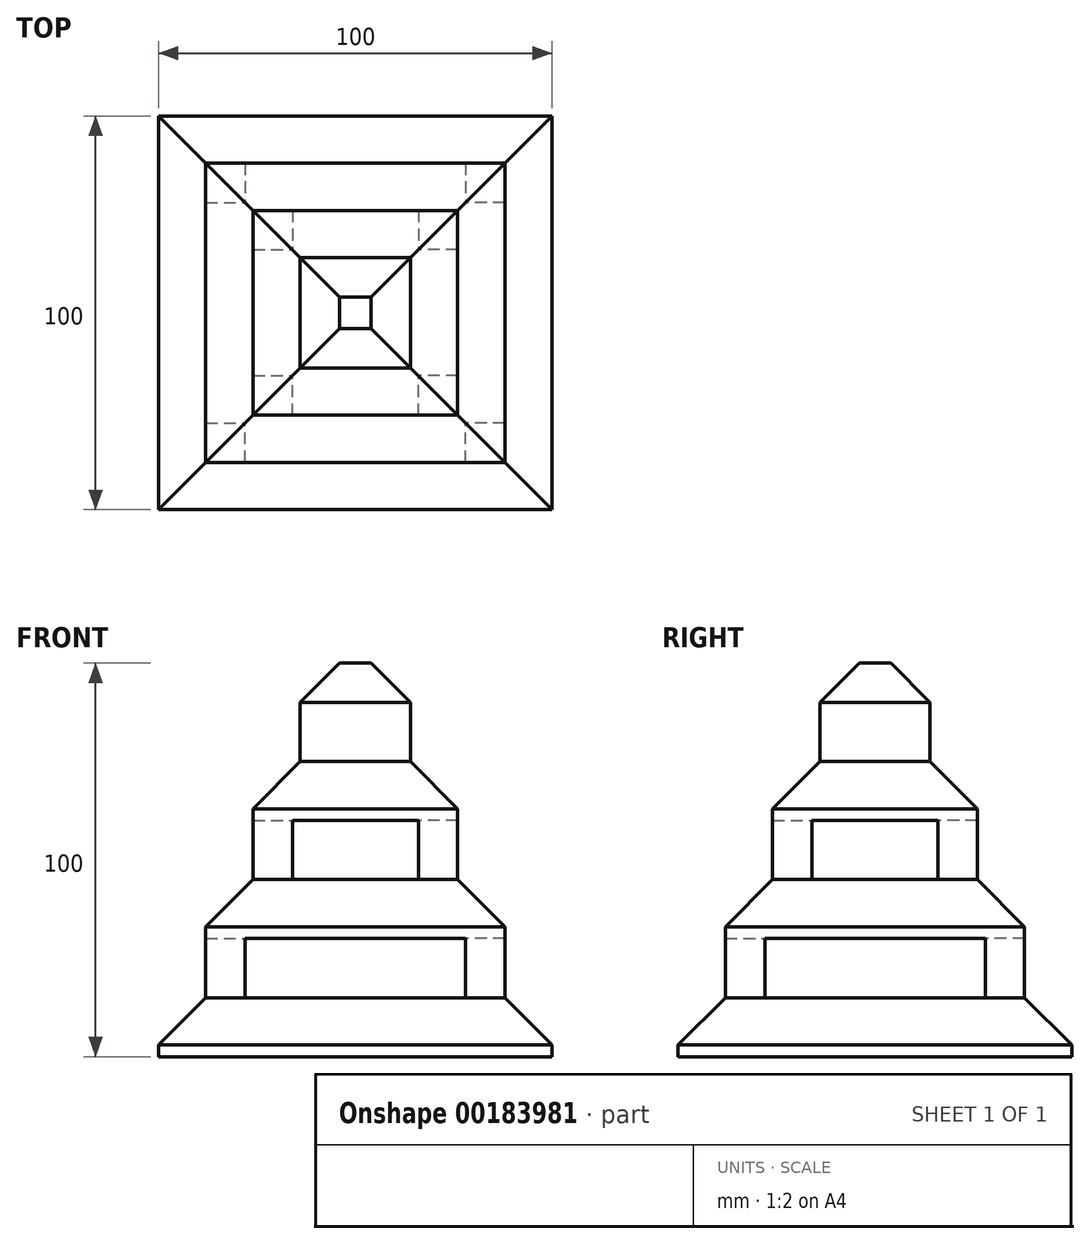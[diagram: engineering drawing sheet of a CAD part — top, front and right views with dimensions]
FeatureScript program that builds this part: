
annotation { "Feature Type Name" : "Feature", "Feature Type Description" : "" }
export const myFeature = defineFeature(function(context is Context, id is Id, definition is map)
    precondition{}
    {
        {
            var Q0;
            Q0=qCreatedBy(makeId("Top.planeOp"),FACE);
            var sketch = newSketch(context, id + "F0", { "sketchPlane" : qUnion([Q0])});
            skLineSegment(sketch, "E0.bottom", {"start": v(-50, 50) * mm, "end": v(50, 50) * mm});
            skLineSegment(sketch, "E0.top", {"start": v(-50, -50) * mm, "end": v(50, -50) * mm});
            skLineSegment(sketch, "E0.left", {"start": v(-50, 50) * mm, "end": v(-50, -50) * mm});
            skLineSegment(sketch, "E0.right", {"start": v(50, 50) * mm, "end": v(50, -50) * mm});
            skPoint(sketch, "E0.middle", {"position": v(0, 0) * mm});
            skSolve(sketch);
        }
        {
            var Q0;
            Q0 = qSketchRegion(id + "F0", true);
            extrude(context, id + "F1", {"entities" : qUnion([Q0]), "depth" : 15 * mm});
        }
        {
            var Q0;
            Q0=makeQuery(id+"F1.opExtrude","CAP_FACE",FACE,{"disambiguationData":[OSD([sQuery(id+"F0.wireOp",EDGE,"E0.bottom"),sQuery(id+"F0.wireOp",EDGE,"E0.top"),sQuery(id+"F0.wireOp",EDGE,"E0.left"),sQuery(id+"F0.wireOp",EDGE,"E0.right")])],"isStart":false});
            chamfer(context, id + "F2", {"entities" : qUnion([Q0]), "width" : 12 * mm, "tangentPropagation" : true});
        }
        {
            var Q0;
            Q0=makeQuery(id+"F1.opExtrude","CAP_FACE",FACE,{"disambiguationData":[OSD([sQuery(id+"F0.wireOp",EDGE,"E0.bottom"),sQuery(id+"F0.wireOp",EDGE,"E0.top"),sQuery(id+"F0.wireOp",EDGE,"E0.left"),sQuery(id+"F0.wireOp",EDGE,"E0.right")])],"isStart":false});
            var sketch = newSketch(context, id + "F3", { "sketchPlane" : qUnion([Q0])});
            skLineSegment(sketch, "E1.bottom", {"start": v(-38, 38) * mm, "end": v(-28, 38) * mm});
            skLineSegment(sketch, "E1.top", {"start": v(-38, 28) * mm, "end": v(-28, 28) * mm});
            skLineSegment(sketch, "E1.left", {"start": v(-38, 38) * mm, "end": v(-38, 28) * mm});
            skLineSegment(sketch, "E1.right", {"start": v(-28, 38) * mm, "end": v(-28, 28) * mm});
            skLineSegment(sketch, "E2.bottom", {"start": v(38, 38) * mm, "end": v(28, 38) * mm});
            skLineSegment(sketch, "E2.top", {"start": v(38, 28) * mm, "end": v(28, 28) * mm});
            skLineSegment(sketch, "E2.left", {"start": v(38, 38) * mm, "end": v(38, 28) * mm});
            skLineSegment(sketch, "E2.right", {"start": v(28, 38) * mm, "end": v(28, 28) * mm});
            skLineSegment(sketch, "E3.bottom", {"start": v(38, -38) * mm, "end": v(28, -38) * mm});
            skLineSegment(sketch, "E3.top", {"start": v(38, -28) * mm, "end": v(28, -28) * mm});
            skLineSegment(sketch, "E3.left", {"start": v(38, -38) * mm, "end": v(38, -28) * mm});
            skLineSegment(sketch, "E3.right", {"start": v(28, -38) * mm, "end": v(28, -28) * mm});
            skLineSegment(sketch, "E4.bottom", {"start": v(-38, -38) * mm, "end": v(-28, -38) * mm});
            skLineSegment(sketch, "E4.top", {"start": v(-38, -28) * mm, "end": v(-28, -28) * mm});
            skLineSegment(sketch, "E4.left", {"start": v(-38, -38) * mm, "end": v(-38, -28) * mm});
            skLineSegment(sketch, "E4.right", {"start": v(-28, -38) * mm, "end": v(-28, -28) * mm});
            skSolve(sketch);
        }
        {
            var Q0;
            Q0=makeQuery(id+"F3.imprint","IMPRINT",FACE,{"disambiguationData":[TD([[makeQuery(id+"F3.imprint","IMPRINT",EDGE,{"derivedFrom":sQuery(id+"F3.wireOp",EDGE,"E1.bottom")}),1.0]])]});
            var Q1;
            Q1=makeQuery(id+"F3.imprint","IMPRINT",FACE,{"disambiguationData":[TD([[makeQuery(id+"F3.imprint","IMPRINT",EDGE,{"derivedFrom":sQuery(id+"F3.wireOp",EDGE,"E2.bottom")}),1.0]])]});
            var Q2;
            Q2=makeQuery(id+"F3.imprint","IMPRINT",FACE,{"disambiguationData":[TD([[makeQuery(id+"F3.imprint","IMPRINT",EDGE,{"derivedFrom":sQuery(id+"F3.wireOp",EDGE,"E3.bottom")}),1.0]])]});
            var Q3;
            Q3=makeQuery(id+"F3.imprint","IMPRINT",FACE,{"disambiguationData":[TD([[makeQuery(id+"F3.imprint","IMPRINT",EDGE,{"derivedFrom":sQuery(id+"F3.wireOp",EDGE,"E4.bottom")}),1.0]])]});
            extrude(context, id + "F4", {"entities" : qUnion([Q0, Q1, Q2, Q3]), "operationType" : NewBodyOperationType.ADD, "depth" : 15 * mm});
        }
        {
            var Q0;
            Q0=makeQuery(id+"F4.opExtrude","CAP_FACE",FACE,{"disambiguationData":[OSD([sQuery(id+"F3.wireOp",EDGE,"E1.bottom"),sQuery(id+"F3.wireOp",EDGE,"E1.top"),sQuery(id+"F3.wireOp",EDGE,"E1.left"),sQuery(id+"F3.wireOp",EDGE,"E1.right")])],"isStart":false});
            var sketch = newSketch(context, id + "F5", { "sketchPlane" : qUnion([Q0])});
            skLineSegment(sketch, "E5.bottom", {"start": v(-38, 38) * mm, "end": v(38, 38) * mm});
            skLineSegment(sketch, "E5.top", {"start": v(-38, -38) * mm, "end": v(38, -38) * mm});
            skLineSegment(sketch, "E5.left", {"start": v(-38, 38) * mm, "end": v(-38, -38) * mm});
            skLineSegment(sketch, "E5.right", {"start": v(38, 38) * mm, "end": v(38, -38) * mm});
            skSolve(sketch);
        }
        {
            var Q0;
            {var subQ3=sQuery(id+"F5.wireOp",EDGE,"E5.top");Q0=makeQuery(id+"F5.imprint","IMPRINT",FACE,{"disambiguationData":[TD([[makeQuery(id+"F5.imprint","IMPRINT",EDGE,{"derivedFrom":subQ3}),1.0]])]});}
            var Q1;
            {var subQ4=makeQuery(id+"F4.opExtrude","CAP_EDGE",EDGE,{"disambiguationData":[OSD([sQuery(id+"F3.wireOp",EDGE,"E1.top")])],"isStart":false});Q1=makeQuery(id+"F5.imprint","IMPRINT",FACE,{"disambiguationData":[TD([[makeQuery(id+"F5.imprint","IMPRINT",EDGE,{"derivedFrom":subQ4}),1.0]])]});}
            extrude(context, id + "F6", {"entities" : qUnion([Q0, Q1]), "operationType" : NewBodyOperationType.ADD, "depth" : 15 * mm});
        }
        {
            var Q0;
            Q0=makeQuery(id+"F6.opExtrude","CAP_FACE",FACE,{"disambiguationData":[OSD([sQuery(id+"F5.wireOp",EDGE,"E5.bottom"),sQuery(id+"F5.wireOp",EDGE,"E5.top"),sQuery(id+"F5.wireOp",EDGE,"E5.left"),sQuery(id+"F5.wireOp",EDGE,"E5.right")])],"isStart":false});
            chamfer(context, id + "F7", {"entities" : qUnion([Q0]), "width" : 12 * mm, "tangentPropagation" : true});
        }
        {
            var Q0;
            Q0=makeQuery(id+"F6.opExtrude","CAP_FACE",FACE,{"disambiguationData":[OSD([sQuery(id+"F5.wireOp",EDGE,"E5.bottom"),sQuery(id+"F5.wireOp",EDGE,"E5.top"),sQuery(id+"F5.wireOp",EDGE,"E5.left"),sQuery(id+"F5.wireOp",EDGE,"E5.right")])],"isStart":false});
            var sketch = newSketch(context, id + "F8", { "sketchPlane" : qUnion([Q0])});
            skLineSegment(sketch, "E6.bottom", {"start": v(26, 26) * mm, "end": v(16, 26) * mm});
            skLineSegment(sketch, "E6.top", {"start": v(26, 16) * mm, "end": v(16, 16) * mm});
            skLineSegment(sketch, "E6.left", {"start": v(26, 26) * mm, "end": v(26, 16) * mm});
            skLineSegment(sketch, "E6.right", {"start": v(16, 26) * mm, "end": v(16, 16) * mm});
            skLineSegment(sketch, "E7.bottom", {"start": v(26, -26) * mm, "end": v(16, -26) * mm});
            skLineSegment(sketch, "E7.top", {"start": v(26, -16) * mm, "end": v(16, -16) * mm});
            skLineSegment(sketch, "E7.left", {"start": v(26, -26) * mm, "end": v(26, -16) * mm});
            skLineSegment(sketch, "E7.right", {"start": v(16, -26) * mm, "end": v(16, -16) * mm});
            skLineSegment(sketch, "E8.bottom", {"start": v(-26, -26) * mm, "end": v(-16, -26) * mm});
            skLineSegment(sketch, "E8.top", {"start": v(-26, -16) * mm, "end": v(-16, -16) * mm});
            skLineSegment(sketch, "E8.left", {"start": v(-26, -26) * mm, "end": v(-26, -16) * mm});
            skLineSegment(sketch, "E8.right", {"start": v(-16, -26) * mm, "end": v(-16, -16) * mm});
            skLineSegment(sketch, "E9.bottom", {"start": v(-26, 26) * mm, "end": v(-16, 26) * mm});
            skLineSegment(sketch, "E9.top", {"start": v(-26, 16) * mm, "end": v(-16, 16) * mm});
            skLineSegment(sketch, "E9.left", {"start": v(-26, 26) * mm, "end": v(-26, 16) * mm});
            skLineSegment(sketch, "E9.right", {"start": v(-16, 26) * mm, "end": v(-16, 16) * mm});
            skSolve(sketch);
        }
        {
            var Q0;
            Q0=makeQuery(id+"F8.imprint","IMPRINT",FACE,{"disambiguationData":[TD([[makeQuery(id+"F8.imprint","IMPRINT",EDGE,{"derivedFrom":sQuery(id+"F8.wireOp",EDGE,"E9.bottom")}),1.0]])]});
            var Q1;
            Q1=makeQuery(id+"F8.imprint","IMPRINT",FACE,{"disambiguationData":[TD([[makeQuery(id+"F8.imprint","IMPRINT",EDGE,{"derivedFrom":sQuery(id+"F8.wireOp",EDGE,"E6.bottom")}),1.0]])]});
            var Q2;
            Q2=makeQuery(id+"F8.imprint","IMPRINT",FACE,{"disambiguationData":[TD([[makeQuery(id+"F8.imprint","IMPRINT",EDGE,{"derivedFrom":sQuery(id+"F8.wireOp",EDGE,"E7.bottom")}),1.0]])]});
            var Q3;
            Q3=makeQuery(id+"F8.imprint","IMPRINT",FACE,{"disambiguationData":[TD([[makeQuery(id+"F8.imprint","IMPRINT",EDGE,{"derivedFrom":sQuery(id+"F8.wireOp",EDGE,"E8.bottom")}),1.0]])]});
            extrude(context, id + "F9", {"entities" : qUnion([Q0, Q1, Q2, Q3]), "operationType" : NewBodyOperationType.ADD, "depth" : 15 * mm});
        }
        {
            var Q0;
            Q0=makeQuery(id+"F9.opExtrude","CAP_FACE",FACE,{"disambiguationData":[OSD([sQuery(id+"F8.wireOp",EDGE,"E9.bottom"),sQuery(id+"F8.wireOp",EDGE,"E9.top"),sQuery(id+"F8.wireOp",EDGE,"E9.left"),sQuery(id+"F8.wireOp",EDGE,"E9.right")])],"isStart":false});
            var sketch = newSketch(context, id + "F10", { "sketchPlane" : qUnion([Q0])});
            skLineSegment(sketch, "E10.bottom", {"start": v(-26, 26) * mm, "end": v(26, 26) * mm});
            skLineSegment(sketch, "E10.top", {"start": v(-26, -26) * mm, "end": v(26, -26) * mm});
            skLineSegment(sketch, "E10.left", {"start": v(-26, 26) * mm, "end": v(-26, -26) * mm});
            skLineSegment(sketch, "E10.right", {"start": v(26, 26) * mm, "end": v(26, -26) * mm});
            skSolve(sketch);
        }
        {
            var Q0;
            Q0 = qSketchRegion(id + "F10", true);
            extrude(context, id + "F11", {"entities" : qUnion([Q0]), "operationType" : NewBodyOperationType.ADD, "depth" : 15 * mm});
        }
        {
            var Q0;
            Q0=makeQuery(id+"F11.opExtrude","CAP_FACE",FACE,{"disambiguationData":[OSD([sQuery(id+"F10.wireOp",EDGE,"E10.bottom"),sQuery(id+"F10.wireOp",EDGE,"E10.top"),sQuery(id+"F10.wireOp",EDGE,"E10.left"),sQuery(id+"F10.wireOp",EDGE,"E10.right")])],"isStart":false});
            chamfer(context, id + "F12", {"entities" : qUnion([Q0]), "width" : 12 * mm, "tangentPropagation" : true});
        }
        {
            var Q0;
            Q0=makeQuery(id+"F11.opExtrude","CAP_FACE",FACE,{"disambiguationData":[OSD([sQuery(id+"F10.wireOp",EDGE,"E10.bottom"),sQuery(id+"F10.wireOp",EDGE,"E10.top"),sQuery(id+"F10.wireOp",EDGE,"E10.left"),sQuery(id+"F10.wireOp",EDGE,"E10.right")])],"isStart":false});
            extrude(context, id + "F13", {"entities" : qUnion([Q0]), "operationType" : NewBodyOperationType.ADD, "depth" : 25 * mm});
        }
        {
            var Q0;
            Q0=makeQuery(id+"F13.opExtrude","CAP_FACE",FACE,{"disambiguationData":[OSD([sQuery(id+"F10.wireOp",EDGE,"E10.bottom"),sQuery(id+"F10.wireOp",EDGE,"E10.top"),sQuery(id+"F10.wireOp",EDGE,"E10.left"),sQuery(id+"F10.wireOp",EDGE,"E10.right")])],"isStart":false});
            chamfer(context, id + "F14", {"entities" : qUnion([Q0]), "width" : 10 * mm, "tangentPropagation" : true});
        }
    });
